# Revit family: Módulo aislador de línea_Aguilera Electronica
name_source: partatom
category: Dispositivos de alarma de incendios
revit_build: Autodesk Revit 2017 (Build: 20160225_1515(x64)
units: mm (PartAtom-declared; Revit-internal decimal feet)

## family parameters
Anfitrión = Cara
Compartido = No
Corte con vacíos al cargar = No
Cota de conector redondo = Diámetro de uso
Mantener orientación de anotación = Sí
Número OmniClass = 23.85.30.21
Punto de cálculo de habitación = No
Tipo de pieza = Normal
Título OmniClass = Environmental Detection/Registration

## types (1)
- Módulo aislador de línea
    Descripción = Unidad fabricada por AGUILERA ELECTRÓNICA según norma EN 54-17:2004 Unidad microprocesada que se intercala en un bucle del sistema algorítmico, cada 23 equipos máximo, determinado por normativa EN 54-14, creando sectores. Su función es la de controlar la corriente que circula por el bucle y si esta se incrementa, sobrepasando los parámetros que tiene programados, abre la línea, aislando el resto del bucle para que este siga funcionando.
Cuando la anomalía desaparece se repone automáticamente restableciendo el normal funcionamiento.
• Control de corriente bidireccional.
• Montado en caja de ABS de 105 x 82 x 25mm.
    Diámetro tubo = 20 mm  [stored 0.0656168 ft]
    Elevación por defecto = 1200 mm
    Fabricante = Aguilera Electrónica
    Modelo = AE/SA-AB
    Símbolo = Sí
    Símbolo texto modelo = Sí
    URL = http://aguilera.es

note: [stored X ft] marks values corroborated as IEEE doubles in the binary element streams (Revit-internal decimal feet)
